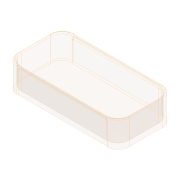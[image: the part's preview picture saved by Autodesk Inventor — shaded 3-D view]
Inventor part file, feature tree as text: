
AUTODESK INVENTOR PART (.ipt)
format: ipt  version: 2022 (Build 260153000, 153)  size: 208,384 bytes
history: mixed  units: mm
features: fillet x1, imported_body x1
ambient origin geometry x8: Origin, YZ Plane, XZ Plane, XY Plane, X Axis, Y Axis, Z Axis, Center Point
bodies: Volumenkörper4 (imported_parasolid)
feature tree (2):
  fillet  "Fillet38"  [1 undecoded]
  imported_body  NMx_Import_Brep_tag  [imported B-rep: ~21 faces, bbox_mm=[298.0, 2.0, 146.0]]
note: 1 required parameter value undecoded (feature->parameter linkage not recoverable at this tier; creation-order binding heuristic only, values carry confidence <= 0.55)
